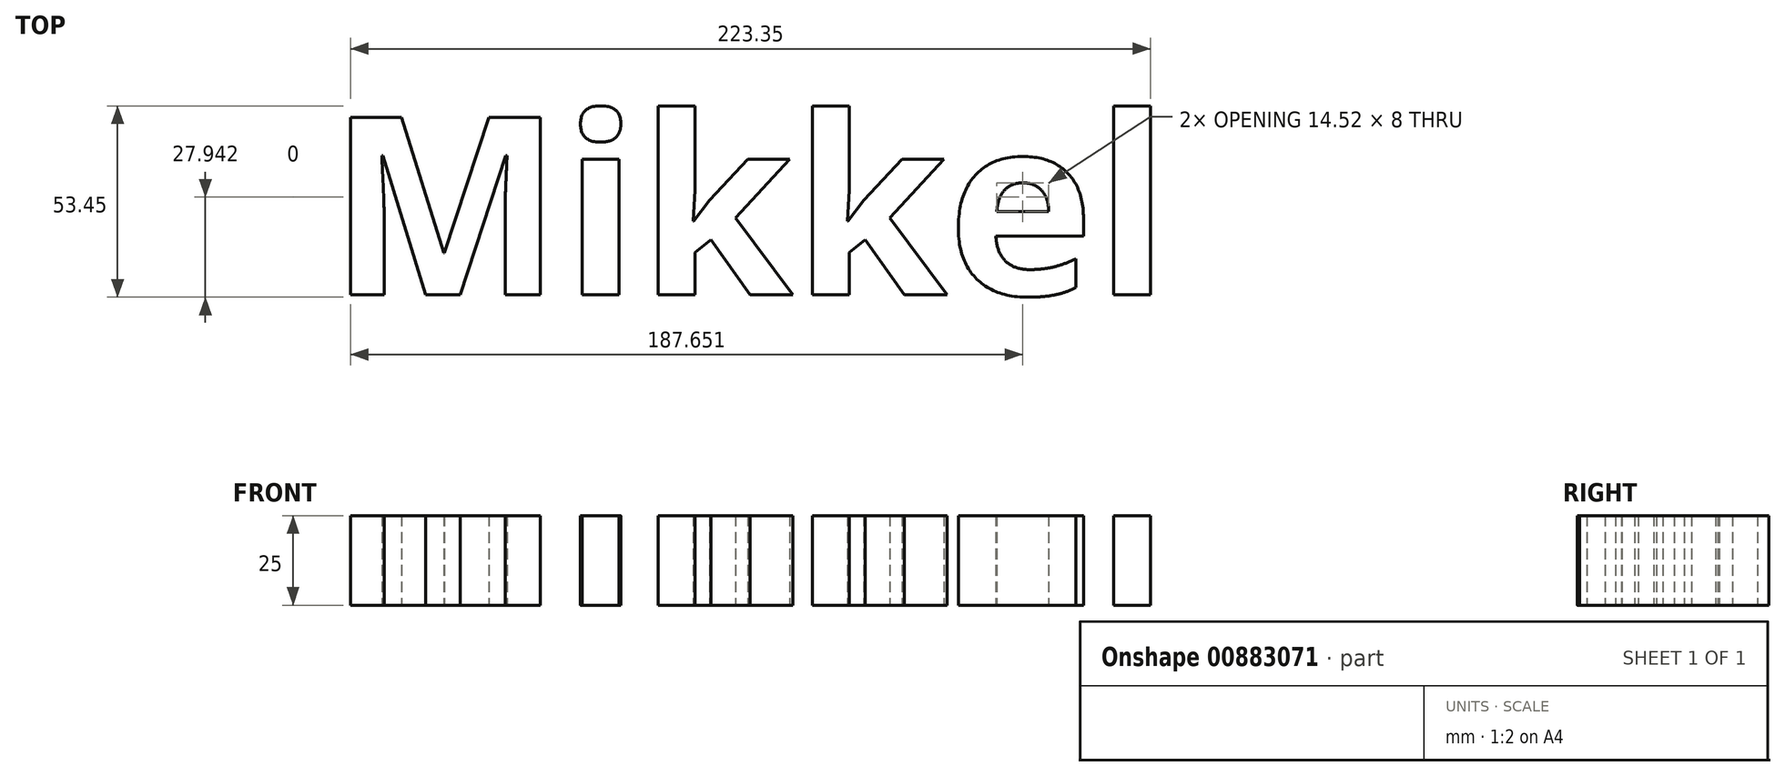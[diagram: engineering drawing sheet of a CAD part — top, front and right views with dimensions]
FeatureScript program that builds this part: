
annotation { "Feature Type Name" : "Feature", "Feature Type Description" : "" }
export const myFeature = defineFeature(function(context is Context, id is Id, definition is map)
    precondition{}
    {
        {
            var Q0;
            Q0=qCreatedBy(makeId("Top.planeOp"),FACE);
            var sketch = newSketch(context, id + "F0", { "sketchPlane" : qUnion([Q0])});
            skText(sketch, "E0", { "text": "Mikkel", "fontName": "AllertaStencil-Regular.ttf"});
            skText(sketch, "E1", { "text": "Mikkel", "fontName": "Arimo-Regular.ttf"});
            skText(sketch, "E2", { "text": "Mikkel", "fontName": "RobotoSlab-Regular.ttf"});
            skText(sketch, "E3", { "text": "Mikkel", "fontName": "RobotoSlab-Regular.ttf"});
            skText(sketch, "E4", { "text": "Mikkel", "fontName": "Tinos-Regular.ttf"});
            skText(sketch, "E5", { "text": "Mikkel", "fontName": "NotoSans-Bold.ttf"});
            skText(sketch, "E6", { "text": "Mikkel", "fontName": "RobotoSlab-Regular.ttf"});
            skText(sketch, "E7", { "text": "Mikkel", "fontName": "RobotoSlab-Regular.ttf"});
            skText(sketch, "E8", { "text": "Mikkel", "fontName": "RobotoSlab-Regular.ttf"});
            skLineSegment(sketch, "E9", {"start": v(0, -25) * mm, "end": v(0, -30) * mm, "construction": true});
            skLineSegment(sketch, "E10", {"start": v(0, -80) * mm, "end": v(0, -85) * mm, "construction": true});
            const initialGuessF0  = {"E0": [-0.1148, -0.025, 1, 0, 0.05], "E1": [-0.09847, -0.08, 1, 0, 0.05], "E2": [-0.12888, -0.14023, 1, 0, 0.05523], "E3": [-0.11195, -0.19044, 1, 0, 0.04798], "E4": [-0.11897, -0.26445, 1, 0, 0.05845], "E5": [-0.12875, -0.45667, 1, 0, 0.05], "E6": [-0.07161, -0.53667, 1, 0, 0.05], "E7": [-0.03406, -0.67217, 1, 0, 0.05], "E8": [-0.0357, -0.76686, 1, 0, 0.05]};
            skSetInitialGuess(sketch, initialGuessF0);
            skSolve(sketch);
        }
        {
            var Q0;
            Q0=makeQuery(id+"F0.imprint","IMPRINT",FACE,{"disambiguationData":[TD([[makeQuery(id+"F0.imprint","IMPRINT",EDGE,{"derivedFrom":sQuery(id+"F0.wireOp",EDGE,"E5.sketch_text.stroke-0")}),-1.0]])]});
            var Q1;
            Q1=makeQuery(id+"F0.imprint","IMPRINT",FACE,{"disambiguationData":[TD([[makeQuery(id+"F0.imprint","IMPRINT",EDGE,{"derivedFrom":sQuery(id+"F0.wireOp",EDGE,"E5.sketch_text.stroke-24")}),-1.0]])]});
            var Q2;
            Q2=makeQuery(id+"F0.imprint","IMPRINT",FACE,{"disambiguationData":[TD([[makeQuery(id+"F0.imprint","IMPRINT",EDGE,{"derivedFrom":sQuery(id+"F0.wireOp",EDGE,"E5.sketch_text.stroke-19")}),-1.0]])]});
            var Q3;
            Q3=makeQuery(id+"F0.imprint","IMPRINT",FACE,{"disambiguationData":[TD([[makeQuery(id+"F0.imprint","IMPRINT",EDGE,{"derivedFrom":sQuery(id+"F0.wireOp",EDGE,"E5.sketch_text.stroke-28")}),-1.0]])]});
            var Q4;
            Q4=makeQuery(id+"F0.imprint","IMPRINT",FACE,{"disambiguationData":[TD([[makeQuery(id+"F0.imprint","IMPRINT",EDGE,{"derivedFrom":sQuery(id+"F0.wireOp",EDGE,"E5.sketch_text.stroke-43")}),-1.0]])]});
            var Q5;
            Q5=makeQuery(id+"F0.imprint","IMPRINT",FACE,{"disambiguationData":[TD([[makeQuery(id+"F0.imprint","IMPRINT",EDGE,{"derivedFrom":sQuery(id+"F0.wireOp",EDGE,"E5.sketch_text.stroke-58")}),-1.0]])]});
            var Q6;
            Q6=makeQuery(id+"F0.imprint","IMPRINT",FACE,{"disambiguationData":[TD([[makeQuery(id+"F0.imprint","IMPRINT",EDGE,{"derivedFrom":sQuery(id+"F0.wireOp",EDGE,"E5.sketch_text.stroke-78")}),-1.0]])]});
            extrude(context, id + "F1", {"entities" : qUnion([Q0, Q1, Q2, Q3, Q4, Q5, Q6]), "depth" : 25 * mm, "offsetDistance" : 25 * mm});
        }
    });
